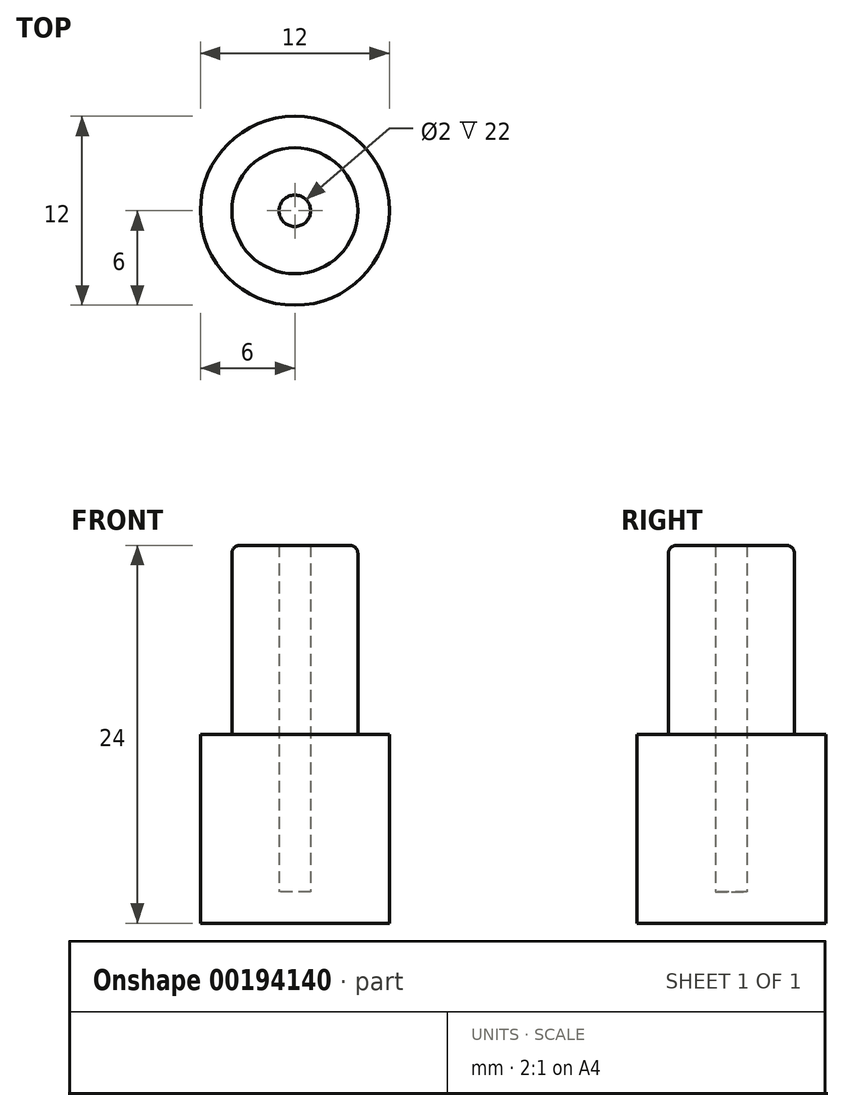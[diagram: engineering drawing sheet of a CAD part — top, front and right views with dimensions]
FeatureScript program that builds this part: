
annotation { "Feature Type Name" : "Feature", "Feature Type Description" : "" }
export const myFeature = defineFeature(function(context is Context, id is Id, definition is map)
    precondition{}
    {
        {
            var Q0;
            Q0=qCreatedBy(makeId("Top.planeOp"),FACE);
            var sketch = newSketch(context, id + "F0", { "sketchPlane" : qUnion([Q0])});
            skCircle(sketch, "E0", {"center": v(0, 0) * mm, "radius": 6 * mm});
            skCircle(sketch, "E1", {"center": v(0, 0) * mm, "radius": 4 * mm});
            skCircle(sketch, "E2", {"center": v(0, 0) * mm, "radius": 1 * mm});
            skSolve(sketch);
        }
        {
            var Q0;
            Q0=makeQuery(id+"F0.imprint","IMPRINT",FACE,{"disambiguationData":[TD([[makeQuery(id+"F0.imprint","IMPRINT",EDGE,{"derivedFrom":sQuery(id+"F0.wireOp",EDGE,"E2")}),1.0]])]});
            extrude(context, id + "F1", {"entities" : qUnion([Q0]), "depth" : 2 * mm});
        }
        {
            var Q0;
            Q0=makeQuery(id+"F0.imprint","IMPRINT",FACE,{"disambiguationData":[TD([[makeQuery(id+"F0.imprint","IMPRINT",EDGE,{"derivedFrom":sQuery(id+"F0.wireOp",EDGE,"E1")}),1.0]])]});
            extrude(context, id + "F2", {"entities" : qUnion([Q0]), "operationType" : NewBodyOperationType.ADD, "depth" : 24 * mm});
        }
        {
            var Q0;
            Q0=makeQuery(id+"F0.imprint","IMPRINT",FACE,{"disambiguationData":[TD([[makeQuery(id+"F0.imprint","IMPRINT",EDGE,{"derivedFrom":sQuery(id+"F0.wireOp",EDGE,"E0")}),1.0]])]});
            extrude(context, id + "F3", {"entities" : qUnion([Q0]), "operationType" : NewBodyOperationType.ADD, "depth" : 12 * mm});
        }
        {
            var Q0;
            Q0=makeQuery(id+"F2.opExtrude","CAP_EDGE",EDGE,{"disambiguationData":[OSD([sQuery(id+"F0.wireOp",EDGE,"E1")])],"isStart":false});
            fillet(context, id + "F4", {"entities" : qUnion([Q0]), "radius" : 0.5 * mm, "tangentPropagation" : true, "allowEdgeOverflow" : false});
        }
    });
